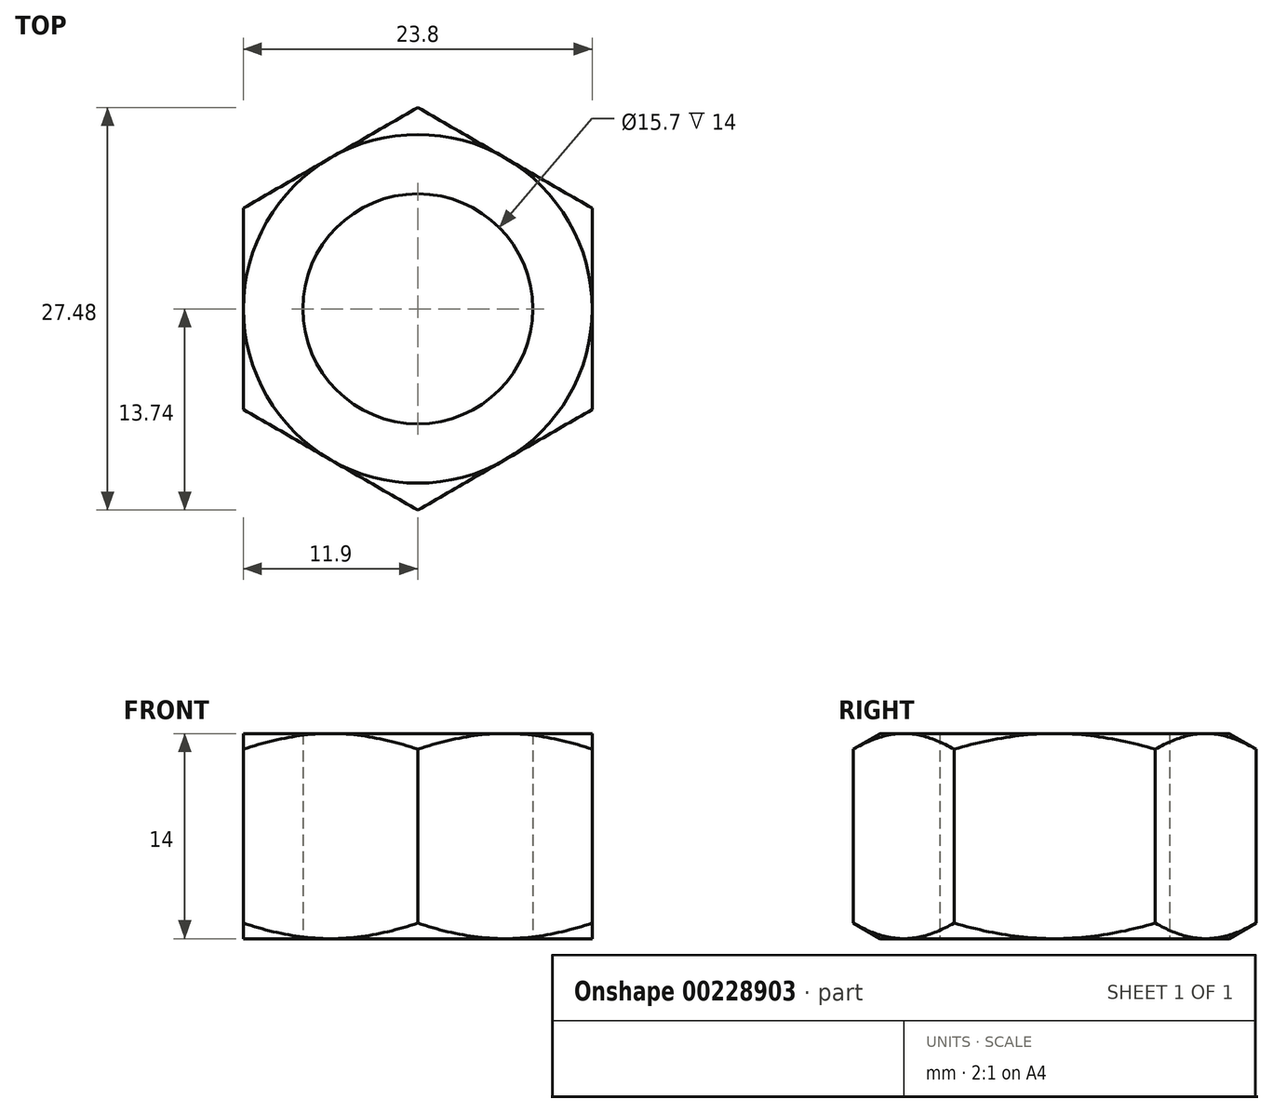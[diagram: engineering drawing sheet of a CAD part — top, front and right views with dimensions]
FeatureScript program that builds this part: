
annotation { "Feature Type Name" : "Feature", "Feature Type Description" : "" }
export const myFeature = defineFeature(function(context is Context, id is Id, definition is map)
    precondition{}
    {
        {
            var Q0;
            Q0=qCreatedBy(makeId("Top.planeOp"),FACE);
            var sketch = newSketch(context, id + "F0", { "sketchPlane" : qUnion([Q0])});
            skCircle(sketch, "E0.cCircle", {"center": v(0, 0) * mm, "radius": 11.9 * mm, "construction": true});
            skLineSegment(sketch, "E0.0", {"start": v(11.9, 6.87) * mm, "end": v(11.9, -6.87) * mm});
            skLineSegment(sketch, "E0.1", {"start": v(11.9, -6.87) * mm, "end": v(0, -13.74) * mm});
            skLineSegment(sketch, "E0.2", {"start": v(0, -13.74) * mm, "end": v(-11.9, -6.87) * mm});
            skLineSegment(sketch, "E0.3", {"start": v(-11.9, -6.87) * mm, "end": v(-11.9, 6.87) * mm});
            skLineSegment(sketch, "E0.4", {"start": v(-11.9, 6.87) * mm, "end": v(0, 13.74) * mm});
            skLineSegment(sketch, "E0.5", {"start": v(0, 13.74) * mm, "end": v(11.9, 6.87) * mm});
            skPoint(sketch, "E0.0.midPoint", {"position": v(11.9, 0) * mm});
            skCircle(sketch, "E1", {"center": v(0, 0) * mm, "radius": 7.85 * mm});
            skSolve(sketch);
        }
        {
            var Q0;
            Q0 = qSketchRegion(id + "F0", true);
            extrude(context, id + "F1", {"entities" : qUnion([Q0]), "depth" : 14 * mm});
        }
        {
            var Q0;
            Q0=qCreatedBy(makeId("Front.planeOp"),FACE);
            var sketch = newSketch(context, id + "F2", { "sketchPlane" : qUnion([Q0])});
            skLineSegment(sketch, "E2", {"start": v(0, 0) * mm, "end": v(0, 14) * mm, "construction": true});
            skLineSegment(sketch, "E3", {"start": v(0, 7) * mm, "end": v(11.9, 7) * mm, "construction": true});
            skLineSegment(sketch, "E4", {"start": v(11.9, 14) * mm, "end": v(14.82, 14) * mm});
            skLineSegment(sketch, "E5", {"start": v(14.82, 14) * mm, "end": v(14.82, 12.32) * mm});
            skLineSegment(sketch, "E6", {"start": v(14.82, 12.32) * mm, "end": v(11.9, 14) * mm});
            skLineSegment(sketch, "E7.MirrorCS", {"start": v(14.82, 1.68) * mm, "end": v(11.9, 0) * mm});
            skLineSegment(sketch, "E8.MirrorCS", {"start": v(14.82, 0) * mm, "end": v(14.82, 1.68) * mm});
            skLineSegment(sketch, "E9.MirrorCS", {"start": v(11.9, 0) * mm, "end": v(14.82, 0) * mm});
            skSolve(sketch);
        }
        {
            var Q0;
            Q0=makeQuery(id+"F2.imprint","IMPRINT",FACE,{"disambiguationData":[TD([[makeQuery(id+"F2.imprint","IMPRINT",EDGE,{"derivedFrom":sQuery(id+"F2.wireOp",EDGE,"E4")}),-1.0]])]});
            var Q1;
            Q1=makeQuery(id+"F2.imprint","IMPRINT",FACE,{"disambiguationData":[TD([[makeQuery(id+"F2.imprint","IMPRINT",EDGE,{"derivedFrom":sQuery(id+"F2.wireOp",EDGE,"E7.MirrorCS")}),1.0]])]});
            var Q2;
            Q2=sQuery(id+"F2.wireOp",EDGE,"E2");
            revolve(context, id + "F3", {"operationType" : NewBodyOperationType.REMOVE, "entities" : qUnion([Q0, Q1]), "axis" : qUnion([Q2]), "revolveType" : RevolveType.FULL, "oppositeDirection" : true});
        }
    });
